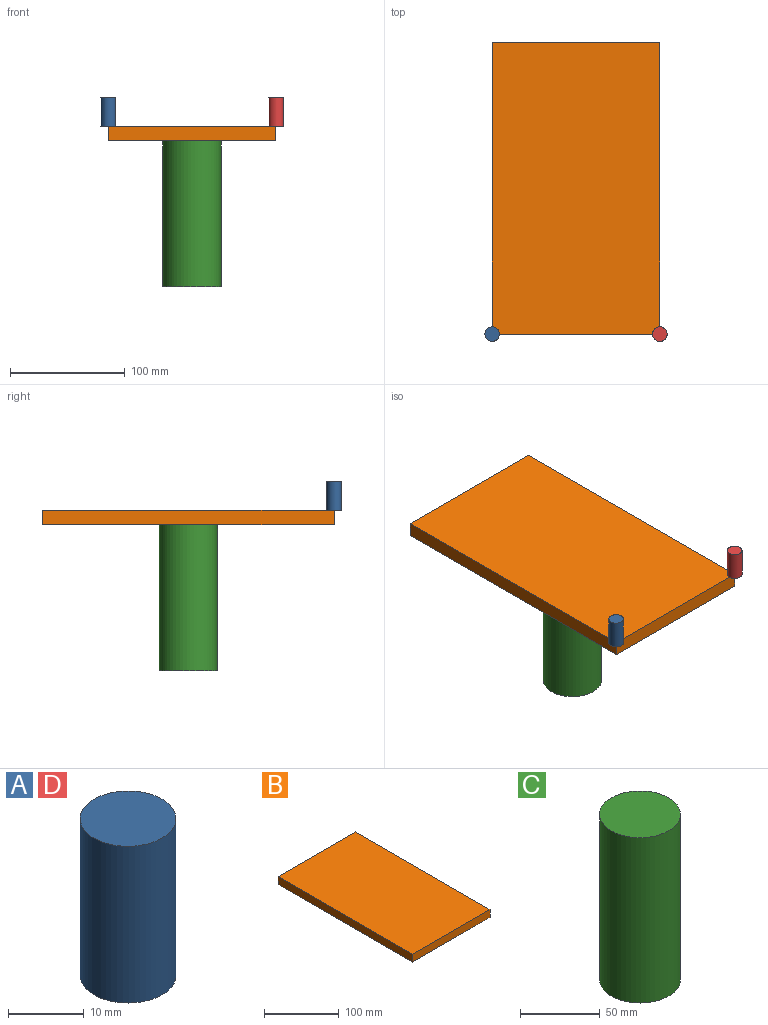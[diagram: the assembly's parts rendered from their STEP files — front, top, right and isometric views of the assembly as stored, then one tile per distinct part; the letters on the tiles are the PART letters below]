
ASSEMBLY  parts=4 mates=3
PART A: 3 faces, bbox 12.7x12.7x25.4 mm
  f0: cylinder r=6.35mm len=25.4mm, axis (0,0,-1), area 1013.4mm2, adj f1,f2
  f1: plane 12.7x12.7mm, normal (0,0,1), area 126.7mm2, adj f0
  f2: plane 12.7x12.7mm, normal (0,0,-1), area 126.7mm2, adj f0
PART B: 6 faces, bbox 146.1x254x12.7 mm
  f0: plane 146.05x12.7mm, normal (0,-1,0), area 1854.8mm2, adj f1,f3,f4,f5
  f1: plane 254x12.7mm, normal (1,0,0), area 3225.8mm2, adj f0,f2,f4,f5
  f2: plane 146.05x12.7mm, normal (0,1,0), area 1854.8mm2, adj f1,f3,f4,f5
  f3: plane 254x12.7mm, normal (-1,0,0), area 3225.8mm2, adj f0,f2,f4,f5
  f4: plane 254x146.05mm, normal (0,0,1), area 37096.7mm2, adj f0,f1,f2,f3
  f5: plane 254x146.05mm, normal (0,0,-1), area 37096.7mm2, adj f0,f1,f2,f3
PART C: 3 faces, bbox 50.8x50.8x127 mm
  f0: cylinder r=25.4mm len=127mm, axis (0,0,-1), area 20268.3mm2, adj f1,f2
  f1: plane 50.8x50.8mm, normal (0,0,1), area 2026.8mm2, adj f0
  f2: plane 50.8x50.8mm, normal (0,0,-1), area 2026.8mm2, adj f0
PART D: same geometry as A
PLACE A t=(-72.1,-76.02,41.76)mm
PLACE B t=(0.92,50.98,22.71)mm
PLACE C t=(0.92,50.98,-47.14)mm
PLACE D t=(73.95,-76.02,41.76)mm
MATE fastened A.f0 <-> B.f4  axis (0,0,-1) through (-72.1,-76.02,29.06)mm
MATE fastened D.f0 <-> B.f4  axis (0,0,-1) through (73.95,-76.02,29.06)mm
MATE fastened C.f0 <-> B.f5  axis (0,0,1) through (0.92,50.98,16.36)mm
